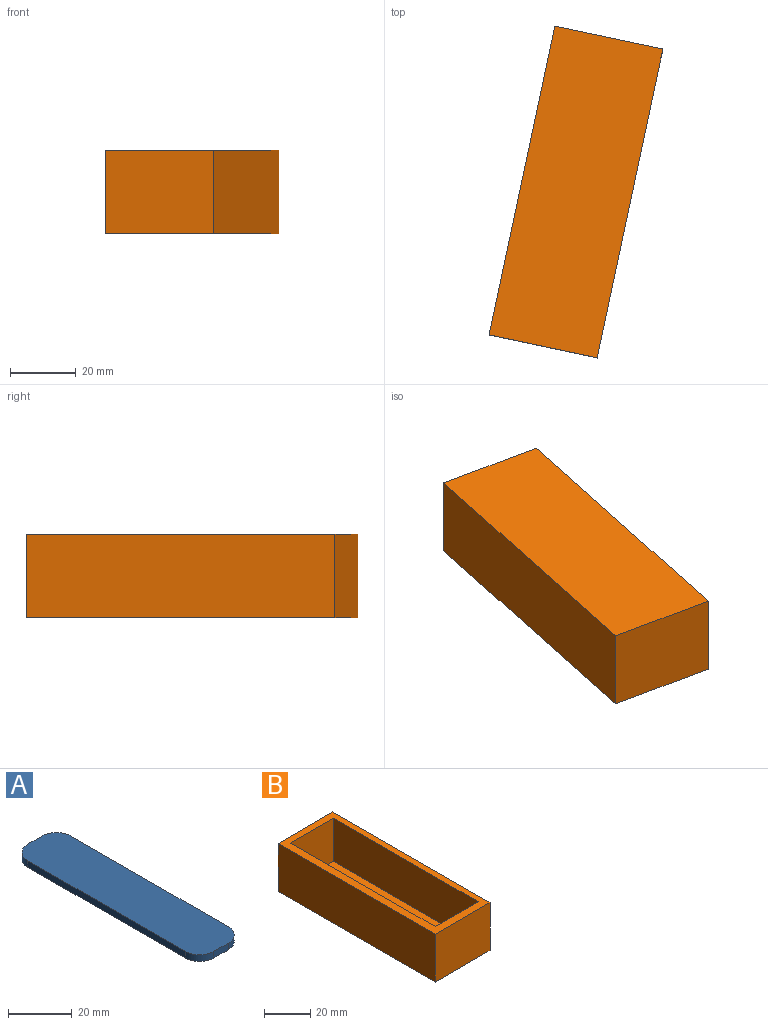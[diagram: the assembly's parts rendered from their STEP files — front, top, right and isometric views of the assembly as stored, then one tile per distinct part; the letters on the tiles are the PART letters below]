
ASSEMBLY  parts=2 mates=1
PART A: 10 faces, bbox 19.1x82.8x2.5 mm
  f0: plane 6.38x2.54mm, normal (0,-1,0), area 16.2mm2, adj f1,f7,f8,f9
  f1: cylinder r=6.35mm len=6.35mm, axis (0,0,-1), area 25.3mm2, adj f0,f2,f8,f9
  f2: plane 70.09x2.54mm, normal (1,0,0), area 178mm2, adj f1,f3,f8,f9
  f3: cylinder r=6.35mm len=6.35mm, axis (0,0,-1), area 25.3mm2, adj f2,f4,f8,f9
  f4: plane 6.38x2.54mm, normal (0,1,0), area 16.2mm2, adj f3,f5,f8,f9
  f5: cylinder r=6.35mm len=6.35mm, axis (0,0,-1), area 25.3mm2, adj f4,f6,f8,f9
  f6: plane 70.09x2.54mm, normal (-1,0,0), area 178mm2, adj f5,f7,f8,f9
  f7: cylinder r=6.35mm len=6.35mm, axis (0,0,-1), area 25.3mm2, adj f0,f6,f8,f9
  f8: plane 82.79x19.08mm, normal (0,0,1), area 1544.6mm2, adj f0,f1,f2,f3,f4,f5,f6,f7
  f9: plane 82.79x19.08mm, normal (0,0,-1), area 1544.6mm2, adj f0,f1,f2,f3,f4,f5,f6,f7
PART B: 11 faces, bbox 33.7x96.3x25.4 mm
  f0: plane 96.29x33.69mm, normal (0,0,1), area 905mm2, adj f1,f2,f3,f4,f6,f7,f8,f9
  f1: plane 33.69x25.4mm, normal (0,1,0), area 855.6mm2, adj f0,f2,f4,f5
  f2: plane 96.29x25.4mm, normal (-1,0,0), area 2445.8mm2, adj f0,f1,f3,f5
  f3: plane 33.69x25.4mm, normal (0,-1,0), area 855.6mm2, adj f0,f2,f4,f5
  f4: plane 96.29x25.4mm, normal (1,0,0), area 2445.8mm2, adj f0,f1,f3,f5
  f5: plane 96.29x33.69mm, normal (0,0,-1), area 3243.6mm2, adj f1,f2,f3,f4
  f6: plane 26.38x22.86mm, normal (0,-1,0), area 603mm2, adj f0,f7,f9,f10
  f7: plane 88.66x22.86mm, normal (1,0,0), area 2026.9mm2, adj f0,f6,f8,f10
  f8: plane 26.38x22.86mm, normal (0,1,0), area 603mm2, adj f0,f7,f9,f10
  f9: plane 88.66x22.86mm, normal (-1,0,0), area 2026.9mm2, adj f0,f6,f8,f10
  f10: plane 88.66x26.38mm, normal (0,0,1), area 2338.7mm2, adj f6,f7,f8,f9
PLACE A rot(axis=(0,0,1),165deg) t=(-37.21,-112.55,-1.45)mm
PLACE B rot(axis=(-0.99,0.1,0),180deg) t=(-40.53,-120.98,3.63)mm fixed
MATE planar A.f8 <-> B.f10  axis (0,0,-1) through (-63.18,-80.06,1.09)mm
